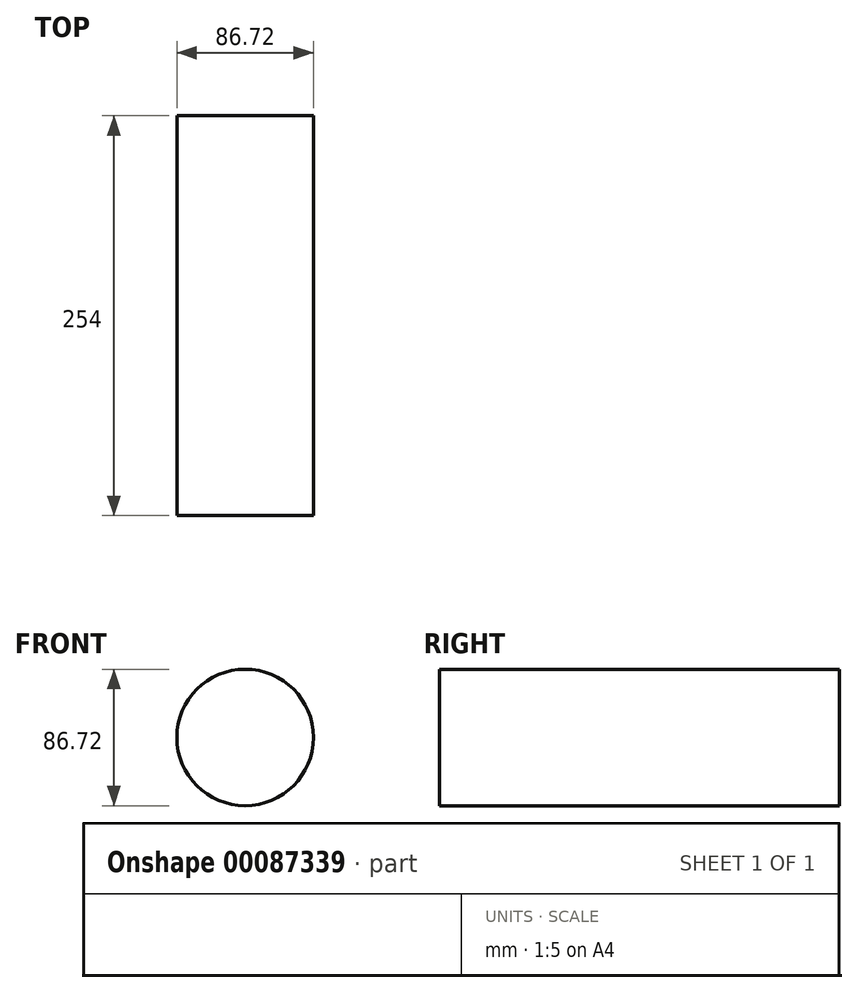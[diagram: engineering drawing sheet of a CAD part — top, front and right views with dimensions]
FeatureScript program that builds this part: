
annotation { "Feature Type Name" : "Feature", "Feature Type Description" : "" }
export const myFeature = defineFeature(function(context is Context, id is Id, definition is map)
    precondition{}
    {
        {
            var Q0;
            Q0=qCreatedBy(makeId("Front.planeOp"),FACE);
            var sketch = newSketch(context, id + "F0", { "sketchPlane" : qUnion([Q0])});
            skCircle(sketch, "E0", {"center": v(0, 0) * mm, "radius": 43.36 * mm});
            skSolve(sketch);
        }
        {
            var Q0;
            Q0=makeQuery(id+"F0.imprint","IMPRINT",FACE,{"disambiguationData":[TD([[makeQuery(id+"F0.imprint","IMPRINT",EDGE,{"derivedFrom":sQuery(id+"F0.wireOp",EDGE,"E0")}),1.0]])]});
            extrude(context, id + "F1", {"entities" : qUnion([Q0]), "depth" : 254 * mm});
        }
    });
